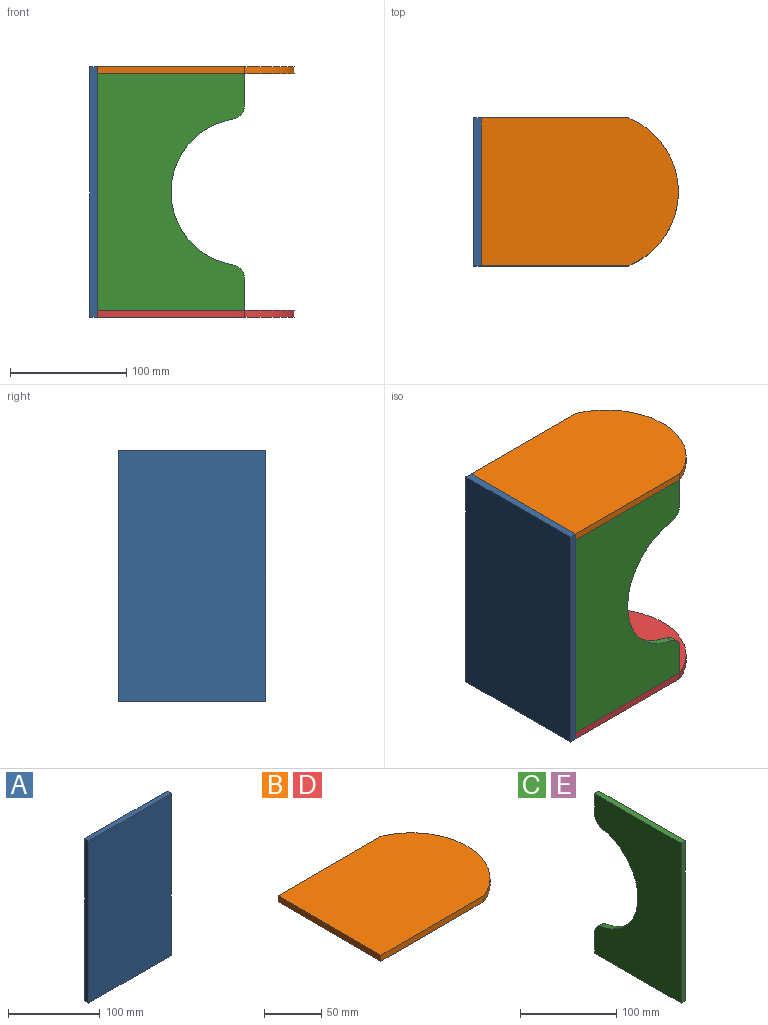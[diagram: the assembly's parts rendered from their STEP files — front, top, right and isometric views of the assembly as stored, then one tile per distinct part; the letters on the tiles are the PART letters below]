
ASSEMBLY  parts=5 mates=12
PART A: 6 faces, bbox 127x6.4x215.9 mm
  f0: plane 215.9x6.35mm, normal (-1,0,0), area 1371mm2, adj f1,f3,f4,f5
  f1: plane 127x6.35mm, normal (0,0,-1), area 806.5mm2, adj f0,f2,f4,f5
  f2: plane 215.9x6.35mm, normal (1,0,0), area 1371mm2, adj f1,f3,f4,f5
  f3: plane 127x6.35mm, normal (0,0,1), area 806.5mm2, adj f0,f2,f4,f5
  f4: plane 215.9x127mm, normal (0,-1,0), area 27419.3mm2, adj f0,f1,f2,f3
  f5: plane 215.9x127mm, normal (0,1,0), area 27419.3mm2, adj f0,f1,f2,f3
PART B: 6 faces, bbox 169.6x127x6.4 mm
  f0: plane 127x6.35mm, normal (0,-1,0), area 806.5mm2, adj f1,f3,f4,f5
  f1: cylinder r=68.6mm len=127mm, axis (0,0,-1), area 1030.4mm2, adj f0,f2,f4,f5
  f2: plane 127x6.35mm, normal (0,1,0), area 806.5mm2, adj f1,f3,f4,f5
  f3: plane 127x6.35mm, normal (-1,0,0), area 806.5mm2, adj f0,f2,f4,f5
  f4: plane 169.64x127mm, normal (0,0,1), area 20046.7mm2, adj f0,f1,f2,f3
  f5: plane 169.64x127mm, normal (0,0,-1), area 20046.7mm2, adj f0,f1,f2,f3
PART C: 10 faces, bbox 6.4x127x203.2 mm
  f0: plane 127x6.35mm, normal (0,0,-1), area 806.5mm2, adj f1,f5,f6,f7
  f1: plane 26.47x6.35mm, normal (0,1,0), area 168.1mm2, adj f0,f6,f7,f8
  f2: cylinder r=63.5mm len=125.22mm, axis (-1,0,0), area 1131.7mm2, adj f6,f7,f8,f9
  f3: plane 26.47x6.35mm, normal (0,1,0), area 168.1mm2, adj f4,f6,f7,f9
  f4: plane 127x6.35mm, normal (0,0,1), area 806.5mm2, adj f3,f5,f6,f7
  f5: plane 203.2x6.35mm, normal (0,-1,0), area 1290.3mm2, adj f0,f4,f6,f7
  f6: plane 203.2x127mm, normal (1,0,0), area 19419.9mm2, adj f0,f1,f2,f3,f4,f5,f8,f9
  f7: plane 203.2x127mm, normal (-1,0,0), area 19419.9mm2, adj f0,f1,f2,f3,f4,f5,f8,f9
  f8: cylinder r=12.7mm len=12.52mm, axis (-1,0,0), area 113.2mm2, adj f1,f2,f6,f7
  f9: cylinder r=12.7mm len=12.52mm, axis (-1,0,0), area 113.2mm2, adj f2,f3,f6,f7
PART D: same geometry as B
PART E: same geometry as C
PLACE A rot(axis=(0.71,0.71,0),180deg) t=(-2.95,-137.45,149.48)mm
PLACE B t=(-2.95,-137.45,143.13)mm
PLACE C rot(axis=(0,0,-1),90deg) t=(-2.95,-131.1,-60.07)mm
PLACE D t=(-2.95,-137.45,-66.42)mm
PLACE E rot(axis=(0,0,-1),90deg) t=(-2.95,-10.45,-60.07)mm
MATE planar B.f0 <-> C.f6  axis (0,-1,0) through (60.55,-137.45,146.31)mm
MATE planar C.f5 <-> D.f3  axis (-1,0,0) through (-2.95,-134.28,41.53)mm
MATE planar E.f5 <-> D.f3  axis (-1,0,0) through (-2.95,-13.63,41.53)mm
MATE planar E.f7 <-> D.f2  axis (0,1,0) through (48.47,-10.45,41.53)mm
MATE planar C.f6 <-> D.f0  axis (0,-1,0) through (60.55,-137.45,-60.07)mm
MATE planar B.f5 <-> E.f4  axis (0,0,-1) through (-2.95,-73.95,143.13)mm
MATE planar A.f5 <-> E.f5  axis (1,0,0) through (-2.95,-73.95,41.53)mm
MATE planar B.f3 <-> E.f5  axis (-1,0,0) through (-2.95,-73.95,146.31)mm
MATE planar A.f0 <-> C.f6  axis (0,-1,0) through (-6.12,-137.45,41.53)mm
MATE planar C.f0 <-> D.f4  axis (0,0,-1) through (60.55,-134.28,-60.07)mm
MATE planar A.f1 <-> B.f4  axis (0,0,1) through (-6.12,-73.95,149.48)mm
MATE planar E.f0 <-> D.f4  axis (0,0,-1) through (60.55,-13.63,-60.07)mm
